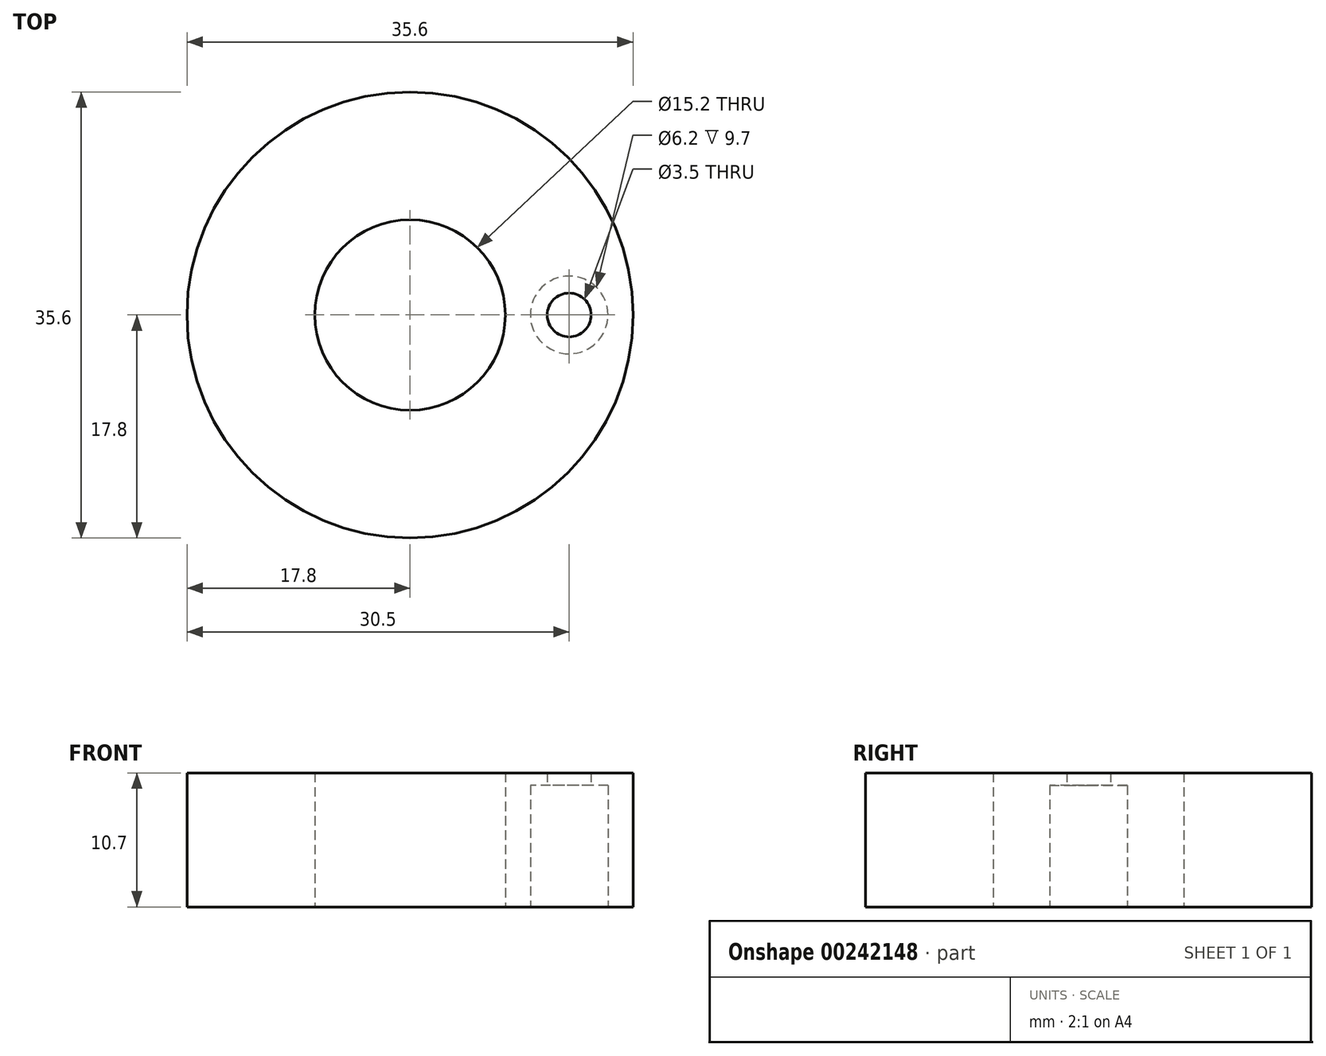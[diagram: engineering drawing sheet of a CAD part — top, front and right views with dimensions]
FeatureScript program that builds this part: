
annotation { "Feature Type Name" : "Feature", "Feature Type Description" : "" }
export const myFeature = defineFeature(function(context is Context, id is Id, definition is map)
    precondition{}
    {
        {
            var Q0;
            Q0=qCreatedBy(makeId("Top.planeOp"),FACE);
            var sketch = newSketch(context, id + "F0", { "sketchPlane" : qUnion([Q0])});
            skCircle(sketch, "E0", {"center": v(0, 0) * mm, "radius": 17.8 * mm});
            skCircle(sketch, "E1", {"center": v(0, 0) * mm, "radius": 7.6 * mm});
            skLineSegment(sketch, "E2", {"start": v(7.6, 0) * mm, "end": v(17.8, 0) * mm, "construction": true});
            skCircle(sketch, "E3", {"center": v(12.7, 0) * mm, "radius": 3.1 * mm});
            skCircle(sketch, "E4", {"center": v(12.7, 0) * mm, "radius": 1.75 * mm});
            skCircle(sketch, "E5", {"center": v(0, 0) * mm, "radius": 12.7 * mm, "construction": true});
            skLineSegment(sketch, "E6", {"start": v(10.95, -2.56) * mm, "end": v(10.95, -3.5) * mm});
            skLineSegment(sketch, "E7", {"start": v(10.95, -3.5) * mm, "end": v(14.45, -3.5) * mm});
            skLineSegment(sketch, "E8", {"start": v(14.45, -3.5) * mm, "end": v(14.45, -2.56) * mm});
            skLineSegment(sketch, "E9", {"start": v(10.95, 2.56) * mm, "end": v(10.95, 3.5) * mm});
            skLineSegment(sketch, "E10", {"start": v(10.95, 3.5) * mm, "end": v(14.45, 3.5) * mm});
            skLineSegment(sketch, "E11", {"start": v(14.45, 3.5) * mm, "end": v(14.45, 2.56) * mm});
            skLineSegment(sketch, "E12", {"start": v(12.7, 3.5) * mm, "end": v(12.7, -3.5) * mm, "construction": true});
            skSolve(sketch);
        }
        {
            var Q0;
            Q0=makeQuery(id+"F0.imprint","IMPRINT",FACE,{"disambiguationData":[TD([[makeQuery(id+"F0.imprint","IMPRINT",EDGE,{"derivedFrom":sQuery(id+"F0.wireOp",EDGE,"E0")}),1.0]])]});
            var Q1;
            Q1=makeQuery(id+"F0.imprint","IMPRINT",FACE,{"disambiguationData":[TD([[makeQuery(id+"F0.imprint","IMPRINT",EDGE,{"derivedFrom":sQuery(id+"F0.wireOp",EDGE,"E3")}),1.0]])]});
            var Q2;
            Q2=makeQuery(id+"F0.imprint","IMPRINT",FACE,{"disambiguationData":[TD([[makeQuery(id+"F0.imprint","IMPRINT",EDGE,{"derivedFrom":sQuery(id+"F0.wireOp",EDGE,"E4")}),1.0]])]});
            var Q3;
            {var subQ0=sQuery(id+"F0.wireOp",EDGE,"E6");Q3=makeQuery(id+"F0.imprint","IMPRINT",FACE,{"disambiguationData":[TD([[makeQuery(id+"F0.imprint","IMPRINT",EDGE,{"derivedFrom":subQ0}),1.0]])]});}
            var Q4;
            {var subQ0=sQuery(id+"F0.wireOp",EDGE,"E9");Q4=makeQuery(id+"F0.imprint","IMPRINT",FACE,{"disambiguationData":[TD([[makeQuery(id+"F0.imprint","IMPRINT",EDGE,{"derivedFrom":subQ0}),-1.0]])]});}
            extrude(context, id + "F1", {"entities" : qUnion([Q0, Q1, Q2, Q3, Q4]), "depth" : 9.7 * mm + 1 * mm});
        }
        {
            var Q0;
            Q0=makeQuery(id+"F0.imprint","IMPRINT",FACE,{"disambiguationData":[TD([[makeQuery(id+"F0.imprint","IMPRINT",EDGE,{"derivedFrom":sQuery(id+"F0.wireOp",EDGE,"E3")}),1.0]])]});
            var Q1;
            Q1=makeQuery(id+"F0.imprint","IMPRINT",FACE,{"disambiguationData":[TD([[makeQuery(id+"F0.imprint","IMPRINT",EDGE,{"derivedFrom":sQuery(id+"F0.wireOp",EDGE,"E4")}),1.0]])]});
            extrude(context, id + "F2", {"entities" : qUnion([Q0, Q1]), "operationType" : NewBodyOperationType.REMOVE, "depth" : 9.7 * mm});
        }
        {
            var Q0;
            Q0=makeQuery(id+"F0.imprint","IMPRINT",FACE,{"disambiguationData":[TD([[makeQuery(id+"F0.imprint","IMPRINT",EDGE,{"derivedFrom":sQuery(id+"F0.wireOp",EDGE,"E4")}),1.0]])]});
            var Q1;
            Q1=makeQuery(id+"F1.opExtrude","CAP_FACE",FACE,{"disambiguationData":[OSD([sQuery(id+"F0.wireOp",EDGE,"E0"),sQuery(id+"F0.wireOp",EDGE,"E1")])],"isStart":false});
            extrude(context, id + "F3", {"entities" : qUnion([Q0]), "operationType" : NewBodyOperationType.REMOVE, "endBound" : BoundingType.UP_TO_SURFACE, "endBoundEntityFace" : qUnion([Q1]), "depth" : 25 * mm});
        }
    });
